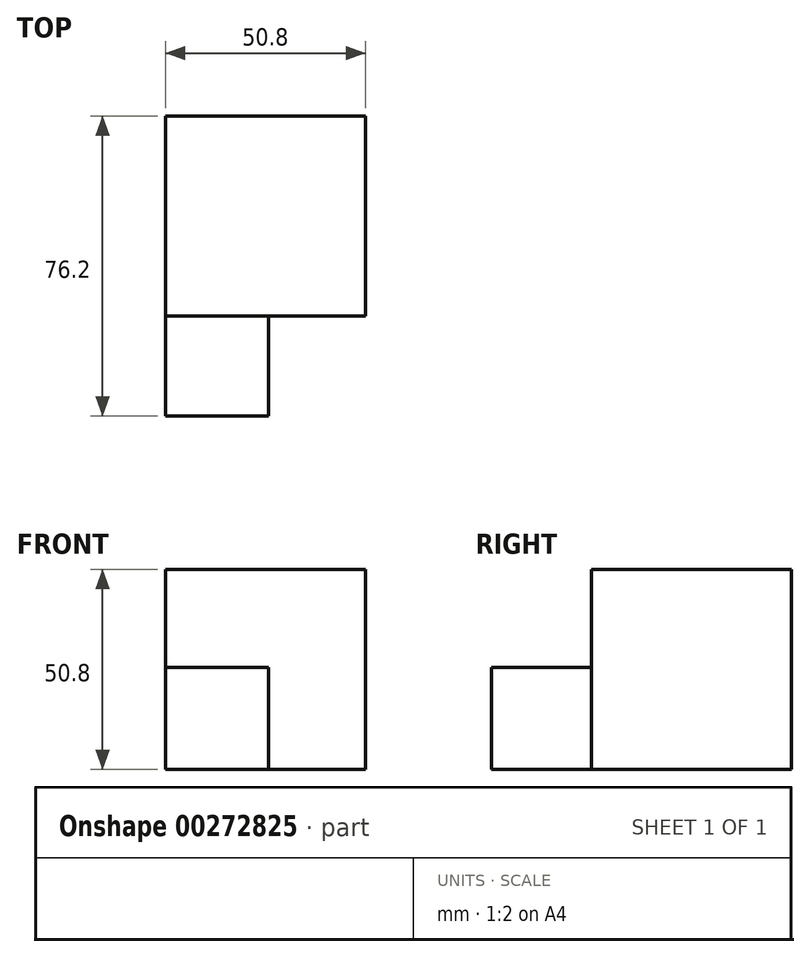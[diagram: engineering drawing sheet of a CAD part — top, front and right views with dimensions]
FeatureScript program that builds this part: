
annotation { "Feature Type Name" : "Feature", "Feature Type Description" : "" }
export const myFeature = defineFeature(function(context is Context, id is Id, definition is map)
    precondition{}
    {
        {
            var Q0;
            Q0=qCreatedBy(makeId("Front.planeOp"),FACE);
            var sketch = newSketch(context, id + "F0", { "sketchPlane" : qUnion([Q0])});
            skLineSegment(sketch, "E0", {"start": v(0, 0) * mm, "end": v(-50.8, 0) * mm});
            skLineSegment(sketch, "E1", {"start": v(-50.8, 0) * mm, "end": v(-50.8, 50.8) * mm});
            skLineSegment(sketch, "E2", {"start": v(-50.8, 50.8) * mm, "end": v(0, 50.8) * mm});
            skLineSegment(sketch, "E3", {"start": v(0, 50.8) * mm, "end": v(0, 0) * mm});
            skSolve(sketch);
        }
        {
            var Q0;
            Q0=makeQuery(id+"F0.imprint","IMPRINT",FACE,{"disambiguationData":[TD([[makeQuery(id+"F0.imprint","IMPRINT",EDGE,{"derivedFrom":sQuery(id+"F0.wireOp",EDGE,"E0")}),-1.0]])]});
            extrude(context, id + "F1", {"entities" : qUnion([Q0]), "depth" : 50.8 * mm});
        }
        {
            var Q0;
            Q0=makeQuery(id+"F1.opExtrude","CAP_FACE",FACE,{"disambiguationData":[OSD([sQuery(id+"F0.wireOp",EDGE,"E0"),sQuery(id+"F0.wireOp",EDGE,"E1"),sQuery(id+"F0.wireOp",EDGE,"E2"),sQuery(id+"F0.wireOp",EDGE,"E3")])],"isStart":false});
            var sketch = newSketch(context, id + "F2", { "sketchPlane" : qUnion([Q0])});
            skLineSegment(sketch, "E4.bottom", {"start": v(-50.8, 0) * mm, "end": v(-24.7, 0) * mm});
            skLineSegment(sketch, "E4.top", {"start": v(-50.8, 25.92) * mm, "end": v(-24.7, 25.92) * mm});
            skLineSegment(sketch, "E4.left", {"start": v(-50.8, 0) * mm, "end": v(-50.8, 25.92) * mm});
            skLineSegment(sketch, "E4.right", {"start": v(-24.7, 0) * mm, "end": v(-24.7, 25.92) * mm});
            skSolve(sketch);
        }
        {
            var Q0;
            Q0 = qSketchRegion(id + "F2", true);
            extrude(context, id + "F3", {"entities" : qUnion([Q0]), "operationType" : NewBodyOperationType.ADD, "depth" : 50.8 * mm});
        }
        {
            var Q0;
            Q0=makeQuery(id+"F3.opExtrude","CAP_FACE",FACE,{"disambiguationData":[OSD([sQuery(id+"F2.wireOp",EDGE,"E4.bottom"),sQuery(id+"F2.wireOp",EDGE,"E4.top"),sQuery(id+"F2.wireOp",EDGE,"E4.left"),sQuery(id+"F2.wireOp",EDGE,"E4.right")])],"isStart":false});
            extrude(context, id + "F4", {"entities" : qUnion([Q0]), "operationType" : NewBodyOperationType.REMOVE, "oppositeDirection" : true, "depth" : 25.4 * mm});
        }
    });
